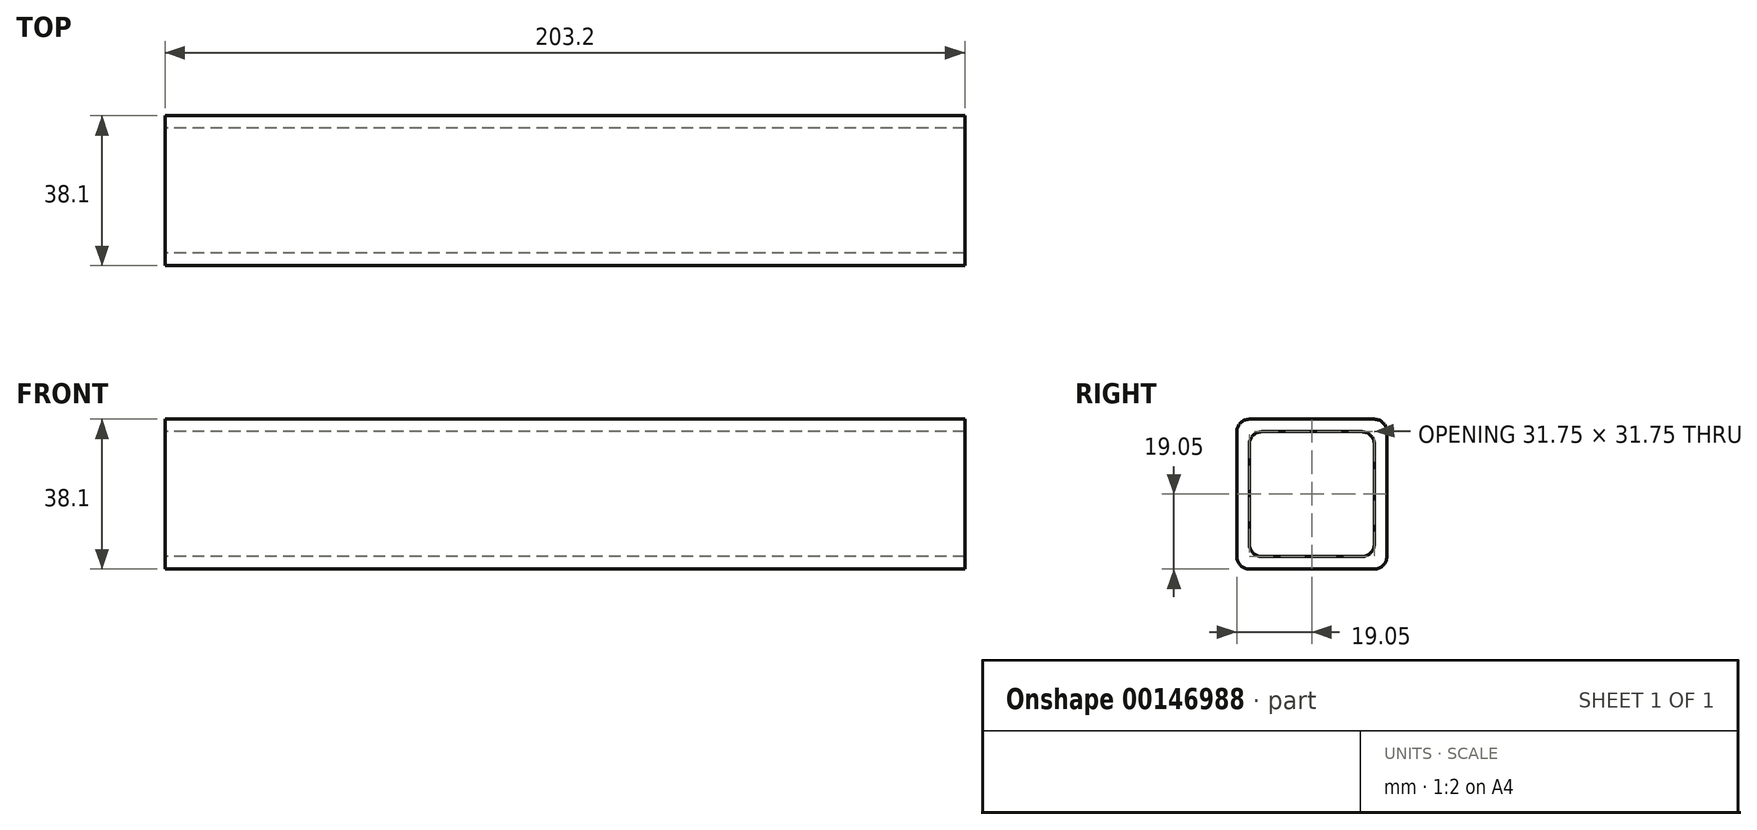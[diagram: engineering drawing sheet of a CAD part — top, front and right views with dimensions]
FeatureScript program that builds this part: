
annotation { "Feature Type Name" : "Feature", "Feature Type Description" : "" }
export const myFeature = defineFeature(function(context is Context, id is Id, definition is map)
    precondition{}
    {
        {
            var Q0;
            Q0=qCreatedBy(makeId("Right.planeOp"),FACE);
            var sketch = newSketch(context, id + "F0", { "sketchPlane" : qUnion([Q0])});
            skLineSegment(sketch, "E0.bottom", {"start": v(15.88, 19.05) * mm, "end": v(-15.88, 19.05) * mm});
            skLineSegment(sketch, "E0.top", {"start": v(15.88, -19.05) * mm, "end": v(-15.87, -19.05) * mm});
            skLineSegment(sketch, "E0.left", {"start": v(19.05, 15.88) * mm, "end": v(19.05, -15.88) * mm});
            skLineSegment(sketch, "E0.right", {"start": v(-19.05, 15.88) * mm, "end": v(-19.05, -15.88) * mm});
            skPoint(sketch, "E0.middle", {"position": v(0, 0) * mm});
            skPoint(sketch, "E1.visualSharp", {"position": v(-19.05, 19.05) * mm});
            skArc(sketch, "E1.filletArc", {"start": v(-15.88, 19.05) * mm, "mid": v(-18.12, 18.12) * mm, "end": v(-19.05, 15.88) * mm});
            skPoint(sketch, "E2.visualSharp", {"position": v(19.05, 19.05) * mm});
            skArc(sketch, "E2.filletArc", {"start": v(19.05, 15.88) * mm, "mid": v(18.12, 18.12) * mm, "end": v(15.88, 19.05) * mm});
            skPoint(sketch, "E3.visualSharp", {"position": v(-19.05, -19.05) * mm});
            skArc(sketch, "E3.filletArc", {"start": v(-19.05, -15.88) * mm, "mid": v(-18.12, -18.12) * mm, "end": v(-15.87, -19.05) * mm});
            skPoint(sketch, "E4.visualSharp", {"position": v(19.05, -19.05) * mm});
            skArc(sketch, "E4.filletArc", {"start": v(15.88, -19.05) * mm, "mid": v(18.12, -18.12) * mm, "end": v(19.05, -15.88) * mm});
            skLineSegment(sketch, "E5.bottom", {"start": v(12.7, 15.88) * mm, "end": v(-12.7, 15.88) * mm});
            skLineSegment(sketch, "E5.top", {"start": v(12.7, -15.88) * mm, "end": v(-12.7, -15.88) * mm});
            skLineSegment(sketch, "E5.left", {"start": v(15.88, 12.7) * mm, "end": v(15.88, -12.7) * mm});
            skLineSegment(sketch, "E5.right", {"start": v(-15.88, 12.7) * mm, "end": v(-15.88, -12.7) * mm});
            skPoint(sketch, "E6.visualSharp", {"position": v(-15.88, 15.87) * mm});
            skArc(sketch, "E6.filletArc", {"start": v(-12.7, 15.88) * mm, "mid": v(-14.95, 14.95) * mm, "end": v(-15.88, 12.7) * mm});
            skPoint(sketch, "E7.visualSharp", {"position": v(15.87, 15.88) * mm});
            skArc(sketch, "E7.filletArc", {"start": v(15.88, 12.7) * mm, "mid": v(14.95, 14.95) * mm, "end": v(12.7, 15.88) * mm});
            skArc(sketch, "E8.filletArc", {"start": v(-15.88, -12.7) * mm, "mid": v(-14.95, -14.95) * mm, "end": v(-12.7, -15.88) * mm});
            skPoint(sketch, "E9.visualSharp", {"position": v(15.88, -15.87) * mm});
            skArc(sketch, "E9.filletArc", {"start": v(12.7, -15.88) * mm, "mid": v(14.95, -14.95) * mm, "end": v(15.88, -12.7) * mm});
            skSolve(sketch);
        }
        {
            var Q0;
            Q0 = qSketchRegion(id + "F0", true);
            extrude(context, id + "F1", {"entities" : qUnion([Q0]), "depth" : 203.2 * mm});
        }
    });
